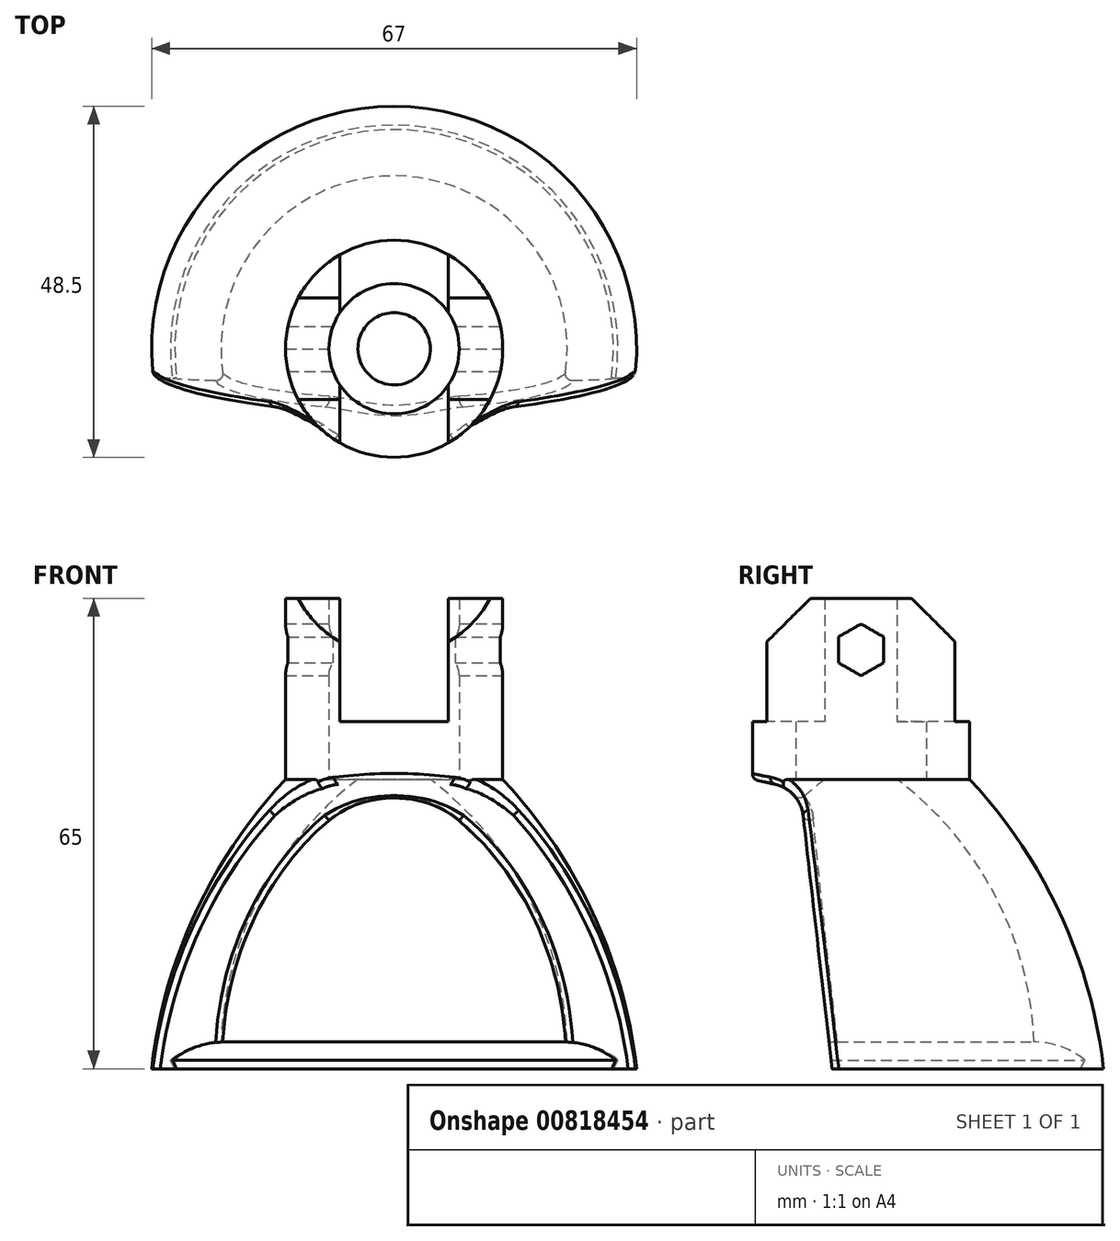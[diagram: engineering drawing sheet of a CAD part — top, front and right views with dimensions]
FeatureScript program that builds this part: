
annotation { "Feature Type Name" : "Feature", "Feature Type Description" : "" }
export const myFeature = defineFeature(function(context is Context, id is Id, definition is map)
    precondition{}
    {
        {
            var Q0;
            Q0=qCreatedBy(makeId("Front.planeOp"),FACE);
            var sketch = newSketch(context, id + "F0", { "sketchPlane" : qUnion([Q0])});
            skLineSegment(sketch, "E0", {"start": v(-15, 40) * mm, "end": v(-5, 40) * mm});
            skLineSegment(sketch, "E1", {"start": v(0, 0) * mm, "end": v(0, 78.33) * mm, "construction": true});
            skLineSegment(sketch, "E2", {"start": v(-33.5, 0) * mm, "end": v(-30.3, 0) * mm});
            skLineSegment(sketch, "E3", {"start": v(-30.3, 0) * mm, "end": v(-30.9, 1.2) * mm});
            skArc(sketch, "E4", {"start": v(-5, 40) * mm, "mid": v(-18.51, 23.97) * mm, "end": v(-23.9, 3.7) * mm});
            skArc(sketch, "E5", {"start": v(-15, 40) * mm, "mid": v(-27.48, 21.5) * mm, "end": v(-33.5, 0) * mm});
            skArc(sketch, "E6", {"start": v(-23.9, 3.7) * mm, "mid": v(-27.62, 3.06) * mm, "end": v(-30.9, 1.2) * mm});
            skLineSegment(sketch, "E7", {"start": v(-23.9, 3.7) * mm, "end": v(0, 3.7) * mm, "construction": true});
            skSolve(sketch);
        }
        {
            var Q0;
            Q0 = qSketchRegion(id + "F0", true);
            var Q1;
            Q1=sQuery(id+"F0.wireOp",EDGE,"E1");
            revolve(context, id + "F1", {"surfaceOperationType" : NewSurfaceOperationType.NEW, "entities" : qUnion([Q0]), "axis" : qUnion([Q1]), "revolveType" : RevolveType.FULL});
        }
        {
            var Q0;
            Q0=makeQuery(id+"F1.opRevolve","SWEPT_FACE",FACE,{"disambiguationData":[OSD([sQuery(id+"F0.wireOp",EDGE,"E0")])]});
            var sketch = newSketch(context, id + "F2", { "sketchPlane" : qUnion([Q0])});
            skCircle(sketch, "E8.0", {"center": v(0, 0) * mm, "radius": 15 * mm});
            skCircle(sketch, "E9", {"center": v(0, 0) * mm, "radius": 9 * mm});
            skSolve(sketch);
        }
        {
            var Q0;
            Q0 = qSketchRegion(id + "F2", true);
            extrude(context, id + "F3", {"entities" : qUnion([Q0]), "operationType" : NewBodyOperationType.ADD, "depth" : 25 * mm, "offsetDistance" : 25 * mm});
        }
        {
            var Q0;
            Q0=qCreatedBy(makeId("Right.planeOp"),FACE);
            var sketch = newSketch(context, id + "F4", { "sketchPlane" : qUnion([Q0])});
            skLineSegment(sketch, "E10", {"start": v(-15, 40) * mm, "end": v(-11.9, 39.32) * mm});
            skLineSegment(sketch, "E11", {"start": v(-8, 35) * mm, "end": v(-4, 0) * mm});
            skLineSegment(sketch, "E12.0", {"start": v(15, 40) * mm, "end": v(-15, 40) * mm});
            skLineSegment(sketch, "E13", {"start": v(0, 40) * mm, "end": v(0, 0) * mm, "construction": true});
            skLineSegment(sketch, "E14", {"start": v(-15, 40) * mm, "end": v(-35.8, 40) * mm});
            skLineSegment(sketch, "E15", {"start": v(-35.8, 40) * mm, "end": v(-35.8, 0) * mm});
            skLineSegment(sketch, "E16", {"start": v(-35.8, 0) * mm, "end": v(-4, 0) * mm});
            skPoint(sketch, "E17.visualSharp", {"position": v(-8.4, 38.55) * mm});
            skArc(sketch, "E17.filletArc", {"start": v(-8, 35) * mm, "mid": v(-9.25, 37.78) * mm, "end": v(-11.9, 39.32) * mm});
            skSolve(sketch);
        }
        {
            var Q0;
            Q0 = qSketchRegion(id + "F4", true);
            extrude(context, id + "F5", {"entities" : qUnion([Q0]), "operationType" : NewBodyOperationType.REMOVE, "endBound" : BoundingType.THROUGH_ALL, "oppositeDirection" : true, "depth" : 40 * mm, "offsetDistance" : 25 * mm, "hasSecondDirection" : true, "secondDirectionBound" : SecondDirectionBoundingType.THROUGH_ALL, "secondDirectionOppositeDirection" : false, "secondDirectionDepth" : 25 * mm});
        }
        {
            var Q0;
            Q0=makeQuery(id+"FTl4cqU1k2aIQqy_1.1.F5.boolean.opBoolean","INTERSECT",EDGE,{"disambiguationData":[OD(1.0)],"derivedFrom":[makeQuery(id+"F1.opRevolve","SWEPT_FACE",FACE,{"disambiguationData":[OSD([sQuery(id+"F0.wireOp",EDGE,"E5")])]}),makeQuery(id+"FTl4cqU1k2aIQqy_1.1.F5.opExtrude","SWEPT_FACE",FACE,{"disambiguationData":[OSD([sQuery(id+"F4.wireOp",EDGE,"E11")])]})]});
            var Q1;
            Q1=makeQuery(id+"F5.boolean.opBoolean","INTERSECT",EDGE,{"disambiguationData":[OD(1.0)],"derivedFrom":[makeQuery(id+"F1.opRevolve","SWEPT_FACE",FACE,{"disambiguationData":[OSD([sQuery(id+"F0.wireOp",EDGE,"E5")])]}),makeQuery(id+"F5.opExtrude","SWEPT_FACE",FACE,{"disambiguationData":[OSD([sQuery(id+"F4.wireOp",EDGE,"E11")])]})]});
            var Q2;
            Q2=makeQuery(id+"F5.boolean.opBoolean","INTERSECT",EDGE,{"disambiguationData":[OD(1.0)],"derivedFrom":[makeQuery(id+"F1.opRevolve","SWEPT_FACE",FACE,{"disambiguationData":[OSD([sQuery(id+"F0.wireOp",EDGE,"E4")])]}),makeQuery(id+"F5.opExtrude","SWEPT_FACE",FACE,{"disambiguationData":[OSD([sQuery(id+"F4.wireOp",EDGE,"E11")])]})]});
            var Q3;
            Q3=makeQuery(id+"FTl4cqU1k2aIQqy_1.1.F5.boolean.opBoolean","INTERSECT",EDGE,{"disambiguationData":[OD(1.0)],"derivedFrom":[makeQuery(id+"F1.opRevolve","SWEPT_FACE",FACE,{"disambiguationData":[OSD([sQuery(id+"F0.wireOp",EDGE,"E4")])]}),makeQuery(id+"FTl4cqU1k2aIQqy_1.1.F5.opExtrude","SWEPT_FACE",FACE,{"disambiguationData":[OSD([sQuery(id+"F4.wireOp",EDGE,"E11")])]})]});
            fillet(context, id + "F6", {"entities" : qUnion([Q0, Q1, Q2, Q3]), "radius" : 1 * mm, "tangentPropagation" : true, "allowEdgeOverflow" : false});
        }
        {
            var Q0;
            Q0=qCreatedBy(makeId("Front.planeOp"),FACE);
            var sketch = newSketch(context, id + "F7", { "sketchPlane" : qUnion([Q0])});
            skLineSegment(sketch, "E18", {"start": v(-14.56, 40.8) * mm, "end": v(15.66, 40.8) * mm, "construction": true});
            skLineSegment(sketch, "E19.bottom", {"start": v(7.5, 65) * mm, "end": v(-7.5, 65) * mm});
            skLineSegment(sketch, "E19.top", {"start": v(7.5, 48) * mm, "end": v(-7.5, 48) * mm});
            skLineSegment(sketch, "E19.left", {"start": v(7.5, 65) * mm, "end": v(7.5, 48) * mm});
            skLineSegment(sketch, "E19.right", {"start": v(-7.5, 65) * mm, "end": v(-7.5, 48) * mm});
            skLineSegment(sketch, "E20", {"start": v(0, 0) * mm, "end": v(0, 90) * mm, "construction": true});
            skSolve(sketch);
        }
        {
            var Q0;
            Q0 = qSketchRegion(id + "F7", true);
            extrude(context, id + "F8", {"entities" : qUnion([Q0]), "operationType" : NewBodyOperationType.REMOVE, "endBound" : BoundingType.THROUGH_ALL, "oppositeDirection" : true, "depth" : 25 * mm, "offsetDistance" : 25 * mm, "hasSecondDirection" : true, "secondDirectionBound" : SecondDirectionBoundingType.THROUGH_ALL, "secondDirectionOppositeDirection" : false, "secondDirectionDepth" : 25 * mm});
        }
        {
            var Q0;
            Q0=qCreatedBy(makeId("Right.planeOp"),FACE);
            var sketch = newSketch(context, id + "F9", { "sketchPlane" : qUnion([Q0])});
            skLineSegment(sketch, "E21", {"start": v(0, 0) * mm, "end": v(0, 64.9) * mm, "construction": true});
            skCircle(sketch, "E22.cCircle", {"center": v(0, 57.9) * mm, "radius": 3.1 * mm, "construction": true});
            skLineSegment(sketch, "E22.0", {"start": v(0, 54.32) * mm, "end": v(-3.1, 56.11) * mm});
            skLineSegment(sketch, "E22.1", {"start": v(-3.1, 56.11) * mm, "end": v(-3.1, 59.69) * mm});
            skLineSegment(sketch, "E22.2", {"start": v(-3.1, 59.69) * mm, "end": v(0, 61.48) * mm});
            skLineSegment(sketch, "E22.3", {"start": v(0, 61.48) * mm, "end": v(3.1, 59.69) * mm});
            skLineSegment(sketch, "E22.4", {"start": v(3.1, 59.69) * mm, "end": v(3.1, 56.11) * mm});
            skLineSegment(sketch, "E22.5", {"start": v(3.1, 56.11) * mm, "end": v(0, 54.32) * mm});
            skPoint(sketch, "E22.0.midPoint", {"position": v(-1.55, 55.22) * mm});
            skLineSegment(sketch, "E23", {"start": v(-13, 59) * mm, "end": v(-7, 65) * mm});
            skLineSegment(sketch, "E24", {"start": v(-7, 65) * mm, "end": v(-13, 65) * mm});
            skLineSegment(sketch, "E25", {"start": v(-13, 65) * mm, "end": v(-13, 59) * mm});
            skLineSegment(sketch, "E26.MirrorCS", {"start": v(13, 59) * mm, "end": v(7, 65) * mm});
            skLineSegment(sketch, "E27.MirrorCS", {"start": v(7, 65) * mm, "end": v(13, 65) * mm});
            skLineSegment(sketch, "E28.MirrorCS", {"start": v(13, 65) * mm, "end": v(13, 59) * mm});
            skSolve(sketch);
        }
        {
            var Q0;
            Q0 = qSketchRegion(id + "F9", true);
            extrude(context, id + "F10", {"entities" : qUnion([Q0]), "operationType" : NewBodyOperationType.REMOVE, "endBound" : BoundingType.THROUGH_ALL, "oppositeDirection" : true, "depth" : 25 * mm, "offsetDistance" : 25 * mm, "hasSecondDirection" : true, "secondDirectionBound" : SecondDirectionBoundingType.THROUGH_ALL, "secondDirectionOppositeDirection" : false, "secondDirectionDepth" : 25 * mm});
        }
    });
